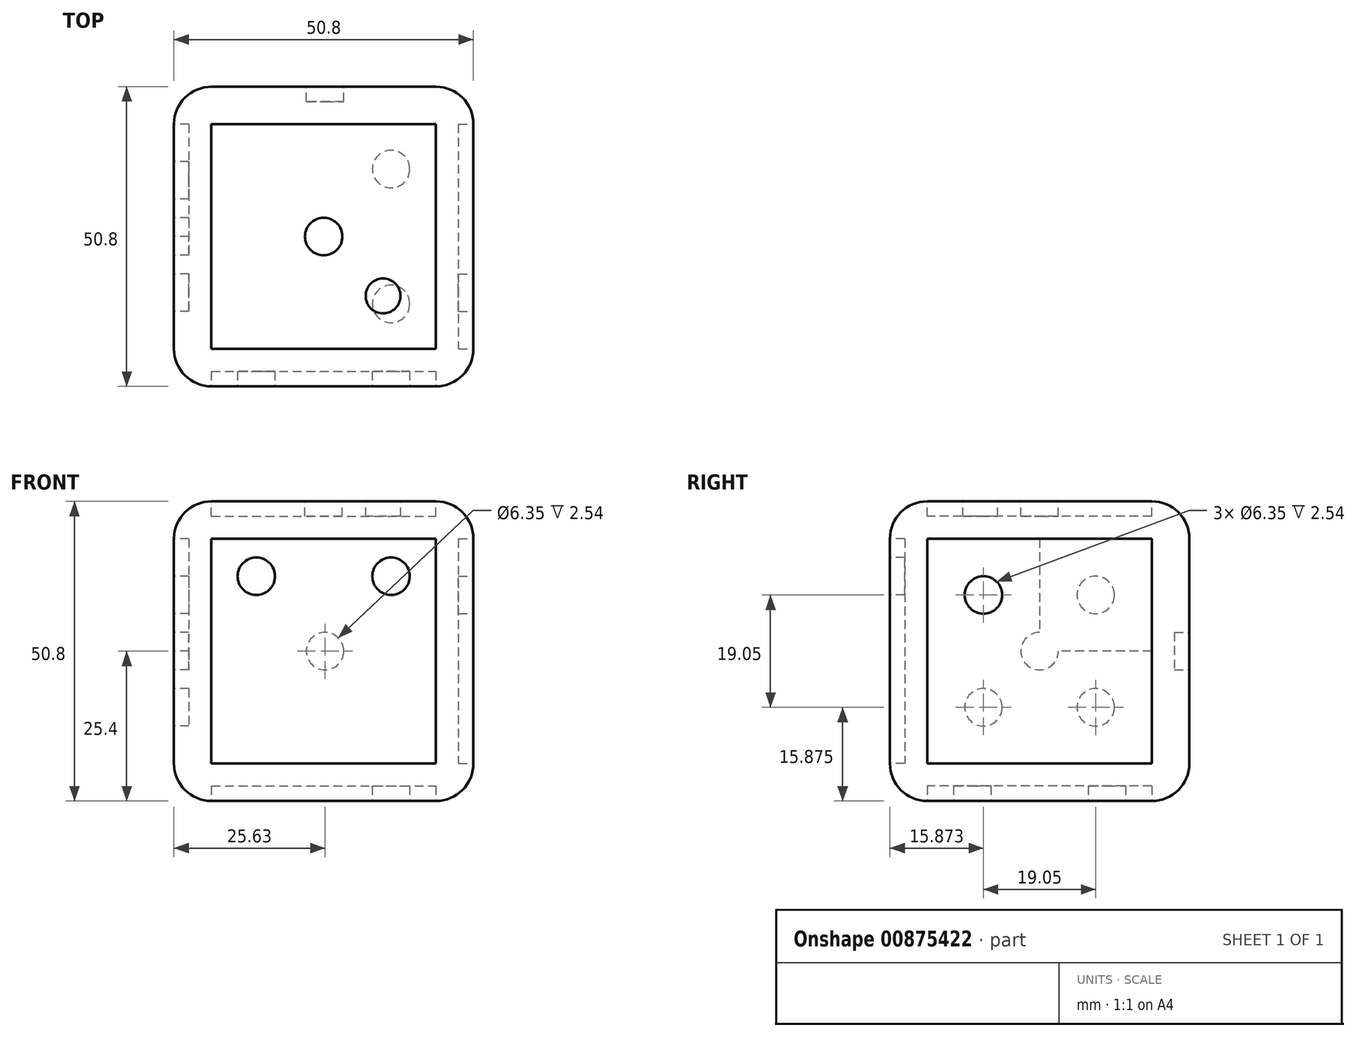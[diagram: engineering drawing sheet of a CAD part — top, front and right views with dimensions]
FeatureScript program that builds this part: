
annotation { "Feature Type Name" : "Feature", "Feature Type Description" : "" }
export const myFeature = defineFeature(function(context is Context, id is Id, definition is map)
    precondition{}
    {
        {
            var Q0;
            Q0=qCreatedBy(makeId("Top.planeOp"),FACE);
            var sketch = newSketch(context, id + "F0", { "sketchPlane" : qUnion([Q0])});
            skLineSegment(sketch, "E0.bottom", {"start": v(-25.63, 43.18) * mm, "end": v(25.17, 43.18) * mm});
            skLineSegment(sketch, "E0.top", {"start": v(-25.63, -7.62) * mm, "end": v(25.17, -7.62) * mm});
            skLineSegment(sketch, "E0.left", {"start": v(-25.63, 43.18) * mm, "end": v(-25.63, -7.62) * mm});
            skLineSegment(sketch, "E0.right", {"start": v(25.17, 43.18) * mm, "end": v(25.17, -7.62) * mm});
            skSolve(sketch);
        }
        {
            var Q0;
            Q0=makeQuery(id+"F0.imprint","IMPRINT",FACE,{"disambiguationData":[TD([[makeQuery(id+"F0.imprint","IMPRINT",EDGE,{"derivedFrom":sQuery(id+"F0.wireOp",EDGE,"E0.bottom")}),-1.0]])]});
            extrude(context, id + "F1", {"entities" : qUnion([Q0]), "depth" : 50.8 * mm, "offsetDistance" : 25.4 * mm});
        }
        {
            var Q0;
            Q0=makeQuery(id+"F1.opExtrude","SWEPT_EDGE",EDGE,{"disambiguationData":[OSD([sQuery(id+"F0.wireOp",EDGE,"E0.top"),sQuery(id+"F0.wireOp",EDGE,"E0.left")])]});
            var Q1;
            Q1=makeQuery(id+"F1.opExtrude","SWEPT_EDGE",EDGE,{"disambiguationData":[OSD([sQuery(id+"F0.wireOp",EDGE,"E0.top"),sQuery(id+"F0.wireOp",EDGE,"E0.right")])]});
            var Q2;
            Q2=makeQuery(id+"F1.opExtrude","CAP_EDGE",EDGE,{"disambiguationData":[OSD([sQuery(id+"F0.wireOp",EDGE,"E0.top")])],"isStart":true});
            var Q3;
            Q3=makeQuery(id+"F1.opExtrude","CAP_EDGE",EDGE,{"disambiguationData":[OSD([sQuery(id+"F0.wireOp",EDGE,"E0.top")])],"isStart":false});
            var Q4;
            Q4=makeQuery(id+"F1.opExtrude","SWEPT_EDGE",EDGE,{"disambiguationData":[OSD([sQuery(id+"F0.wireOp",EDGE,"E0.bottom"),sQuery(id+"F0.wireOp",EDGE,"E0.right")])]});
            var Q5;
            Q5=makeQuery(id+"F1.opExtrude","CAP_EDGE",EDGE,{"disambiguationData":[OSD([sQuery(id+"F0.wireOp",EDGE,"E0.right")])],"isStart":true});
            var Q6;
            Q6=makeQuery(id+"F1.opExtrude","SWEPT_EDGE",EDGE,{"disambiguationData":[OSD([sQuery(id+"F0.wireOp",EDGE,"E0.bottom"),sQuery(id+"F0.wireOp",EDGE,"E0.left")])]});
            var Q7;
            Q7=makeQuery(id+"F1.opExtrude","CAP_EDGE",EDGE,{"disambiguationData":[OSD([sQuery(id+"F0.wireOp",EDGE,"E0.right")])],"isStart":false});
            var Q8;
            Q8=makeQuery(id+"F1.opExtrude","CAP_EDGE",EDGE,{"disambiguationData":[OSD([sQuery(id+"F0.wireOp",EDGE,"E0.bottom")])],"isStart":true});
            var Q9;
            Q9=makeQuery(id+"F1.opExtrude","CAP_EDGE",EDGE,{"disambiguationData":[OSD([sQuery(id+"F0.wireOp",EDGE,"E0.left")])],"isStart":true});
            var Q10;
            Q10=makeQuery(id+"F1.opExtrude","CAP_EDGE",EDGE,{"disambiguationData":[OSD([sQuery(id+"F0.wireOp",EDGE,"E0.left")])],"isStart":false});
            var Q11;
            Q11=makeQuery(id+"F1.opExtrude","CAP_EDGE",EDGE,{"disambiguationData":[OSD([sQuery(id+"F0.wireOp",EDGE,"E0.bottom")])],"isStart":false});
            fillet(context, id + "F2", {"entities" : qUnion([Q0, Q1, Q2, Q3, Q4, Q5, Q6, Q7, Q8, Q9, Q10, Q11]), "radius" : 6.35 * mm, "tangentPropagation" : true, "allowEdgeOverflow" : false});
        }
        {
            var Q0;
            Q0=makeQuery(id+"F1.opExtrude","SWEPT_FACE",FACE,{"disambiguationData":[OSD([sQuery(id+"F0.wireOp",EDGE,"E0.bottom")])]});
            var sketch = newSketch(context, id + "F3", { "sketchPlane" : qUnion([Q0])});
            skLineSegment(sketch, "E1.0.0", {"start": v(-18.82, 44.45) * mm, "end": v(-18.82, 6.35) * mm});
            skLineSegment(sketch, "E1.0.1", {"start": v(-18.82, 6.35) * mm, "end": v(19.28, 6.35) * mm});
            skLineSegment(sketch, "E1.0.2", {"start": v(19.28, 6.35) * mm, "end": v(19.28, 44.45) * mm});
            skLineSegment(sketch, "E1.0.3", {"start": v(19.28, 44.45) * mm, "end": v(-18.82, 44.45) * mm});
            skLineSegment(sketch, "E2", {"start": v(19.28, 25.4) * mm, "end": v(-18.82, 25.4) * mm, "construction": true});
            skLineSegment(sketch, "E3", {"start": v(0, 44.45) * mm, "end": v(0, 6.35) * mm, "construction": true});
            skPoint(sketch, "E3.startSnap0", {"position": v(0.23, 44.45) * mm});
            skCircle(sketch, "E4", {"center": v(0, 25.4) * mm, "radius": 3.18 * mm});
            skSolve(sketch);
        }
        {
            var Q0;
            Q0=makeQuery(id+"F3.imprint","IMPRINT",FACE,{"disambiguationData":[TD([[makeQuery(id+"F3.imprint","IMPRINT",EDGE,{"derivedFrom":sQuery(id+"F3.wireOp",EDGE,"E4")}),1.0]])]});
            var Q1;
            Q1=sQuery(id+"F3.wireOp",EDGE,"E4");
            extrude(context, id + "F4", {"entities" : qUnion([Q0]), "operationType" : NewBodyOperationType.REMOVE, "surfaceEntities" : qUnion([Q1]), "oppositeDirection" : true, "depth" : 2.54 * mm, "offsetDistance" : 25.4 * mm});
        }
        {
            var Q0;
            Q0=makeQuery(id+"F1.opExtrude","SWEPT_FACE",FACE,{"disambiguationData":[OSD([sQuery(id+"F0.wireOp",EDGE,"E0.top")])]});
            var sketch = newSketch(context, id + "F5", { "sketchPlane" : qUnion([Q0])});
            skLineSegment(sketch, "E5.0.0", {"start": v(-19.28, 44.45) * mm, "end": v(-19.28, 6.35) * mm});
            skLineSegment(sketch, "E5.0.1", {"start": v(-19.28, 6.35) * mm, "end": v(18.82, 6.35) * mm});
            skLineSegment(sketch, "E5.0.2", {"start": v(18.82, 6.35) * mm, "end": v(18.82, 44.45) * mm});
            skLineSegment(sketch, "E5.0.3", {"start": v(18.82, 44.45) * mm, "end": v(-19.28, 44.45) * mm});
            skLineSegment(sketch, "E6", {"start": v(-11.66, 44.45) * mm, "end": v(-11.66, 6.35) * mm});
            skLineSegment(sketch, "E7", {"start": v(11.2, 44.45) * mm, "end": v(11.2, 6.35) * mm});
            skCircle(sketch, "E8", {"center": v(-11.66, 38.1) * mm, "radius": 3.18 * mm});
            skCircle(sketch, "E9", {"center": v(-11.66, 25.4) * mm, "radius": 3.18 * mm});
            skCircle(sketch, "E10", {"center": v(-11.66, 12.7) * mm, "radius": 3.18 * mm});
            skCircle(sketch, "E11", {"center": v(11.2, 25.4) * mm, "radius": 3.18 * mm});
            skCircle(sketch, "E12", {"center": v(11.2, 38.1) * mm, "radius": 3.18 * mm});
            skCircle(sketch, "E13", {"center": v(11.2, 12.7) * mm, "radius": 3.18 * mm});
            skSolve(sketch);
        }
        {
            var Q0;
            {var subQ0=sQuery(id+"F5.wireOp",EDGE,"E8");var subQ1=sQuery(id+"F5.wireOp",EDGE,"E6");var subQ2=makeQuery(id+"F5.imprint","INTERSECT",VERTEX,{"disambiguationData":[OD(0.0)],"derivedFrom":[subQ1,subQ0]});Q0=makeQuery(id+"F5.imprint","IMPRINT",FACE,{"disambiguationData":[TD([[makeQuery(id+"F5.imprint","IMPRINT",EDGE,{"disambiguationData":[TD([[subQ2,-1.0]])],"derivedFrom":subQ1}),-1.0]])]});}
            var Q1;
            {var subQ0=sQuery(id+"F5.wireOp",EDGE,"E8");var subQ1=sQuery(id+"F5.wireOp",EDGE,"E6");var subQ2=makeQuery(id+"F5.imprint","INTERSECT",VERTEX,{"disambiguationData":[OD(0.0)],"derivedFrom":[subQ1,subQ0]});Q1=makeQuery(id+"F5.imprint","IMPRINT",FACE,{"disambiguationData":[TD([[makeQuery(id+"F5.imprint","IMPRINT",EDGE,{"disambiguationData":[TD([[subQ2,-1.0]])],"derivedFrom":subQ1}),1.0]])]});}
            var Q2;
            {var subQ0=sQuery(id+"F5.wireOp",EDGE,"E9");var subQ1=sQuery(id+"F5.wireOp",EDGE,"E6");var subQ2=makeQuery(id+"F5.imprint","INTERSECT",VERTEX,{"disambiguationData":[OD(0.0)],"derivedFrom":[subQ1,subQ0]});Q2=makeQuery(id+"F5.imprint","IMPRINT",FACE,{"disambiguationData":[TD([[makeQuery(id+"F5.imprint","IMPRINT",EDGE,{"disambiguationData":[TD([[subQ2,-1.0]])],"derivedFrom":subQ1}),1.0]])]});}
            var Q3;
            {var subQ0=sQuery(id+"F5.wireOp",EDGE,"E9");var subQ1=sQuery(id+"F5.wireOp",EDGE,"E6");var subQ2=makeQuery(id+"F5.imprint","INTERSECT",VERTEX,{"disambiguationData":[OD(0.0)],"derivedFrom":[subQ1,subQ0]});Q3=makeQuery(id+"F5.imprint","IMPRINT",FACE,{"disambiguationData":[TD([[makeQuery(id+"F5.imprint","IMPRINT",EDGE,{"disambiguationData":[TD([[subQ2,-1.0]])],"derivedFrom":subQ1}),-1.0]])]});}
            var Q4;
            {var subQ0=sQuery(id+"F5.wireOp",EDGE,"E10");var subQ1=sQuery(id+"F5.wireOp",EDGE,"E6");var subQ2=makeQuery(id+"F5.imprint","INTERSECT",VERTEX,{"disambiguationData":[OD(0.0)],"derivedFrom":[subQ1,subQ0]});Q4=makeQuery(id+"F5.imprint","IMPRINT",FACE,{"disambiguationData":[TD([[makeQuery(id+"F5.imprint","IMPRINT",EDGE,{"disambiguationData":[TD([[subQ2,-1.0]])],"derivedFrom":subQ1}),1.0]])]});}
            var Q5;
            {var subQ0=sQuery(id+"F5.wireOp",EDGE,"E10");var subQ1=sQuery(id+"F5.wireOp",EDGE,"E6");var subQ2=makeQuery(id+"F5.imprint","INTERSECT",VERTEX,{"disambiguationData":[OD(0.0)],"derivedFrom":[subQ1,subQ0]});Q5=makeQuery(id+"F5.imprint","IMPRINT",FACE,{"disambiguationData":[TD([[makeQuery(id+"F5.imprint","IMPRINT",EDGE,{"disambiguationData":[TD([[subQ2,-1.0]])],"derivedFrom":subQ1}),-1.0]])]});}
            var Q6;
            {var subQ0=sQuery(id+"F5.wireOp",EDGE,"E13");var subQ1=sQuery(id+"F5.wireOp",EDGE,"E7");var subQ2=makeQuery(id+"F5.imprint","INTERSECT",VERTEX,{"disambiguationData":[OD(0.0)],"derivedFrom":[subQ1,subQ0]});Q6=makeQuery(id+"F5.imprint","IMPRINT",FACE,{"disambiguationData":[TD([[makeQuery(id+"F5.imprint","IMPRINT",EDGE,{"disambiguationData":[TD([[subQ2,-1.0]])],"derivedFrom":subQ1}),1.0]])]});}
            var Q7;
            {var subQ0=sQuery(id+"F5.wireOp",EDGE,"E13");var subQ1=sQuery(id+"F5.wireOp",EDGE,"E7");var subQ2=makeQuery(id+"F5.imprint","INTERSECT",VERTEX,{"disambiguationData":[OD(0.0)],"derivedFrom":[subQ1,subQ0]});Q7=makeQuery(id+"F5.imprint","IMPRINT",FACE,{"disambiguationData":[TD([[makeQuery(id+"F5.imprint","IMPRINT",EDGE,{"disambiguationData":[TD([[subQ2,-1.0]])],"derivedFrom":subQ1}),-1.0]])]});}
            var Q8;
            {var subQ0=sQuery(id+"F5.wireOp",EDGE,"E11");var subQ1=sQuery(id+"F5.wireOp",EDGE,"E7");var subQ2=makeQuery(id+"F5.imprint","INTERSECT",VERTEX,{"disambiguationData":[OD(0.0)],"derivedFrom":[subQ1,subQ0]});Q8=makeQuery(id+"F5.imprint","IMPRINT",FACE,{"disambiguationData":[TD([[makeQuery(id+"F5.imprint","IMPRINT",EDGE,{"disambiguationData":[TD([[subQ2,-1.0]])],"derivedFrom":subQ1}),1.0]])]});}
            var Q9;
            {var subQ0=sQuery(id+"F5.wireOp",EDGE,"E11");var subQ1=sQuery(id+"F5.wireOp",EDGE,"E7");var subQ2=makeQuery(id+"F5.imprint","INTERSECT",VERTEX,{"disambiguationData":[OD(0.0)],"derivedFrom":[subQ1,subQ0]});Q9=makeQuery(id+"F5.imprint","IMPRINT",FACE,{"disambiguationData":[TD([[makeQuery(id+"F5.imprint","IMPRINT",EDGE,{"disambiguationData":[TD([[subQ2,-1.0]])],"derivedFrom":subQ1}),-1.0]])]});}
            var Q10;
            {var subQ0=sQuery(id+"F5.wireOp",EDGE,"E12");var subQ1=sQuery(id+"F5.wireOp",EDGE,"E7");var subQ2=makeQuery(id+"F5.imprint","INTERSECT",VERTEX,{"disambiguationData":[OD(0.0)],"derivedFrom":[subQ1,subQ0]});Q10=makeQuery(id+"F5.imprint","IMPRINT",FACE,{"disambiguationData":[TD([[makeQuery(id+"F5.imprint","IMPRINT",EDGE,{"disambiguationData":[TD([[subQ2,-1.0]])],"derivedFrom":subQ1}),1.0]])]});}
            var Q11;
            {var subQ0=sQuery(id+"F5.wireOp",EDGE,"E12");var subQ1=sQuery(id+"F5.wireOp",EDGE,"E7");var subQ2=makeQuery(id+"F5.imprint","INTERSECT",VERTEX,{"disambiguationData":[OD(0.0)],"derivedFrom":[subQ1,subQ0]});Q11=makeQuery(id+"F5.imprint","IMPRINT",FACE,{"disambiguationData":[TD([[makeQuery(id+"F5.imprint","IMPRINT",EDGE,{"disambiguationData":[TD([[subQ2,-1.0]])],"derivedFrom":subQ1}),-1.0]])]});}
            extrude(context, id + "F6", {"entities" : qUnion([Q0, Q1, Q2, Q3, Q4, Q5, Q6, Q7, Q8, Q9, Q10, Q11]), "operationType" : NewBodyOperationType.REMOVE, "oppositeDirection" : true, "depth" : 2.54 * mm, "offsetDistance" : 25.4 * mm});
        }
        {
            var Q0;
            Q0=makeQuery(id+"F1.opExtrude","SWEPT_FACE",FACE,{"disambiguationData":[OSD([sQuery(id+"F0.wireOp",EDGE,"E0.left")])]});
            var sketch = newSketch(context, id + "F7", { "sketchPlane" : qUnion([Q0])});
            skLineSegment(sketch, "E14.0.0", {"start": v(-36.83, 44.45) * mm, "end": v(-36.83, 6.35) * mm});
            skLineSegment(sketch, "E14.0.1", {"start": v(-36.83, 6.35) * mm, "end": v(1.27, 6.35) * mm});
            skLineSegment(sketch, "E14.0.2", {"start": v(1.27, 6.35) * mm, "end": v(1.27, 44.45) * mm});
            skLineSegment(sketch, "E14.0.3", {"start": v(1.27, 44.45) * mm, "end": v(-36.83, 44.45) * mm});
            skLineSegment(sketch, "E15", {"start": v(-36.83, 25.4) * mm, "end": v(1.27, 25.4) * mm});
            skLineSegment(sketch, "E16", {"start": v(1.27, 25.4) * mm, "end": v(-17.78, 25.4) * mm});
            skLineSegment(sketch, "E17", {"start": v(-17.78, 44.45) * mm, "end": v(-17.78, 6.35) * mm});
            skCircle(sketch, "E18", {"center": v(-17.78, 25.4) * mm, "radius": 3.18 * mm});
            skLineSegment(sketch, "E19", {"start": v(-27.3, 44.45) * mm, "end": v(-27.3, 6.35) * mm});
            skLineSegment(sketch, "E20", {"start": v(-8.25, 44.45) * mm, "end": v(-8.25, 6.35) * mm});
            skCircle(sketch, "E21", {"center": v(-27.3, 34.93) * mm, "radius": 3.18 * mm});
            skCircle(sketch, "E22", {"center": v(-27.3, 15.88) * mm, "radius": 3.18 * mm});
            skCircle(sketch, "E23", {"center": v(-8.25, 34.93) * mm, "radius": 3.18 * mm});
            skCircle(sketch, "E24", {"center": v(-8.25, 15.88) * mm, "radius": 3.18 * mm});
            skSolve(sketch);
        }
        {
            var Q0;
            {var subQ0=sQuery(id+"F7.wireOp",EDGE,"E21");var subQ1=sQuery(id+"F7.wireOp",EDGE,"E19");var subQ2=makeQuery(id+"F7.imprint","INTERSECT",VERTEX,{"disambiguationData":[OD(0.0)],"derivedFrom":[subQ1,subQ0]});Q0=makeQuery(id+"F7.imprint","IMPRINT",FACE,{"disambiguationData":[TD([[makeQuery(id+"F7.imprint","IMPRINT",EDGE,{"disambiguationData":[TD([[subQ2,-1.0]])],"derivedFrom":subQ1}),1.0]])]});}
            var Q1;
            {var subQ0=sQuery(id+"F7.wireOp",EDGE,"E21");var subQ1=sQuery(id+"F7.wireOp",EDGE,"E19");var subQ2=makeQuery(id+"F7.imprint","INTERSECT",VERTEX,{"disambiguationData":[OD(0.0)],"derivedFrom":[subQ1,subQ0]});Q1=makeQuery(id+"F7.imprint","IMPRINT",FACE,{"disambiguationData":[TD([[makeQuery(id+"F7.imprint","IMPRINT",EDGE,{"disambiguationData":[TD([[subQ2,-1.0]])],"derivedFrom":subQ1}),-1.0]])]});}
            var Q2;
            {var subQ0=sQuery(id+"F7.wireOp",EDGE,"E23");var subQ1=sQuery(id+"F7.wireOp",EDGE,"E20");var subQ2=makeQuery(id+"F7.imprint","INTERSECT",VERTEX,{"disambiguationData":[OD(0.0)],"derivedFrom":[subQ1,subQ0]});Q2=makeQuery(id+"F7.imprint","IMPRINT",FACE,{"disambiguationData":[TD([[makeQuery(id+"F7.imprint","IMPRINT",EDGE,{"disambiguationData":[TD([[subQ2,-1.0]])],"derivedFrom":subQ1}),-1.0]])]});}
            var Q3;
            {var subQ0=sQuery(id+"F7.wireOp",EDGE,"E23");var subQ1=sQuery(id+"F7.wireOp",EDGE,"E20");var subQ2=makeQuery(id+"F7.imprint","INTERSECT",VERTEX,{"disambiguationData":[OD(0.0)],"derivedFrom":[subQ1,subQ0]});Q3=makeQuery(id+"F7.imprint","IMPRINT",FACE,{"disambiguationData":[TD([[makeQuery(id+"F7.imprint","IMPRINT",EDGE,{"disambiguationData":[TD([[subQ2,-1.0]])],"derivedFrom":subQ1}),1.0]])]});}
            var Q4;
            {var subQ1=sQuery(id+"F7.wireOp",EDGE,"E16");var subQ3=sQuery(id+"F7.wireOp",EDGE,"E18");var subQ4=makeQuery(id+"F7.imprint","INTERSECT",VERTEX,{"derivedFrom":[subQ1,subQ3]});Q4=makeQuery(id+"F7.imprint","IMPRINT",FACE,{"disambiguationData":[TD([[makeQuery(id+"F7.imprint","IMPRINT",EDGE,{"disambiguationData":[TD([[subQ4,-1.0]])],"derivedFrom":subQ3}),1.0]])]});}
            var Q5;
            {var subQ1=sQuery(id+"F7.wireOp",EDGE,"E16");var subQ3=sQuery(id+"F7.wireOp",EDGE,"E18");var subQ4=makeQuery(id+"F7.imprint","INTERSECT",VERTEX,{"derivedFrom":[subQ1,subQ3]});Q5=makeQuery(id+"F7.imprint","IMPRINT",FACE,{"disambiguationData":[TD([[makeQuery(id+"F7.imprint","IMPRINT",EDGE,{"disambiguationData":[TD([[subQ4,1.0]])],"derivedFrom":subQ3}),1.0]])]});}
            var Q6;
            {var subQ1=sQuery(id+"F7.wireOp",EDGE,"E15");var subQ3=sQuery(id+"F7.wireOp",EDGE,"E18");var subQ4=makeQuery(id+"F7.imprint","INTERSECT",VERTEX,{"derivedFrom":[subQ1,subQ3]});Q6=makeQuery(id+"F7.imprint","IMPRINT",FACE,{"disambiguationData":[TD([[makeQuery(id+"F7.imprint","IMPRINT",EDGE,{"disambiguationData":[TD([[subQ4,-1.0]])],"derivedFrom":subQ3}),1.0]])]});}
            var Q7;
            {var subQ1=sQuery(id+"F7.wireOp",EDGE,"E15");var subQ3=sQuery(id+"F7.wireOp",EDGE,"E18");var subQ4=makeQuery(id+"F7.imprint","INTERSECT",VERTEX,{"derivedFrom":[subQ1,subQ3]});Q7=makeQuery(id+"F7.imprint","IMPRINT",FACE,{"disambiguationData":[TD([[makeQuery(id+"F7.imprint","IMPRINT",EDGE,{"disambiguationData":[TD([[subQ4,1.0]])],"derivedFrom":subQ3}),1.0]])]});}
            var Q8;
            {var subQ0=sQuery(id+"F7.wireOp",EDGE,"E24");var subQ1=sQuery(id+"F7.wireOp",EDGE,"E20");var subQ2=makeQuery(id+"F7.imprint","INTERSECT",VERTEX,{"disambiguationData":[OD(0.0)],"derivedFrom":[subQ1,subQ0]});Q8=makeQuery(id+"F7.imprint","IMPRINT",FACE,{"disambiguationData":[TD([[makeQuery(id+"F7.imprint","IMPRINT",EDGE,{"disambiguationData":[TD([[subQ2,-1.0]])],"derivedFrom":subQ1}),1.0]])]});}
            var Q9;
            {var subQ0=sQuery(id+"F7.wireOp",EDGE,"E24");var subQ1=sQuery(id+"F7.wireOp",EDGE,"E20");var subQ2=makeQuery(id+"F7.imprint","INTERSECT",VERTEX,{"disambiguationData":[OD(0.0)],"derivedFrom":[subQ1,subQ0]});Q9=makeQuery(id+"F7.imprint","IMPRINT",FACE,{"disambiguationData":[TD([[makeQuery(id+"F7.imprint","IMPRINT",EDGE,{"disambiguationData":[TD([[subQ2,-1.0]])],"derivedFrom":subQ1}),-1.0]])]});}
            var Q10;
            {var subQ0=sQuery(id+"F7.wireOp",EDGE,"E22");var subQ1=sQuery(id+"F7.wireOp",EDGE,"E19");var subQ2=makeQuery(id+"F7.imprint","INTERSECT",VERTEX,{"disambiguationData":[OD(0.0)],"derivedFrom":[subQ1,subQ0]});Q10=makeQuery(id+"F7.imprint","IMPRINT",FACE,{"disambiguationData":[TD([[makeQuery(id+"F7.imprint","IMPRINT",EDGE,{"disambiguationData":[TD([[subQ2,-1.0]])],"derivedFrom":subQ1}),1.0]])]});}
            var Q11;
            {var subQ0=sQuery(id+"F7.wireOp",EDGE,"E22");var subQ1=sQuery(id+"F7.wireOp",EDGE,"E19");var subQ2=makeQuery(id+"F7.imprint","INTERSECT",VERTEX,{"disambiguationData":[OD(0.0)],"derivedFrom":[subQ1,subQ0]});Q11=makeQuery(id+"F7.imprint","IMPRINT",FACE,{"disambiguationData":[TD([[makeQuery(id+"F7.imprint","IMPRINT",EDGE,{"disambiguationData":[TD([[subQ2,-1.0]])],"derivedFrom":subQ1}),-1.0]])]});}
            extrude(context, id + "F8", {"entities" : qUnion([Q0, Q1, Q2, Q3, Q4, Q5, Q6, Q7, Q8, Q9, Q10, Q11]), "operationType" : NewBodyOperationType.REMOVE, "oppositeDirection" : true, "depth" : 2.54 * mm, "offsetDistance" : 25.4 * mm});
        }
        {
            var Q0;
            Q0=makeQuery(id+"F1.opExtrude","SWEPT_FACE",FACE,{"disambiguationData":[OSD([sQuery(id+"F0.wireOp",EDGE,"E0.right")])]});
            var sketch = newSketch(context, id + "F9", { "sketchPlane" : qUnion([Q0])});
            skLineSegment(sketch, "E25", {"start": v(-1.27, 44.45) * mm, "end": v(36.83, 6.35) * mm});
            skCircle(sketch, "E26", {"center": v(27.3, 15.87) * mm, "radius": 3.18 * mm});
            skCircle(sketch, "E27", {"center": v(8.25, 34.93) * mm, "radius": 3.18 * mm});
            skSolve(sketch);
        }
        {
            var Q0;
            {var subQ0=sQuery(id+"F9.wireOp",EDGE,"E26");var subQ1=sQuery(id+"F9.wireOp",EDGE,"E25");var subQ2=makeQuery(id+"F9.imprint","INTERSECT",VERTEX,{"disambiguationData":[OD(0.0)],"derivedFrom":[subQ1,subQ0]});Q0=makeQuery(id+"F9.imprint","IMPRINT",FACE,{"disambiguationData":[TD([[makeQuery(id+"F9.imprint","IMPRINT",EDGE,{"disambiguationData":[TD([[subQ2,-1.0]])],"derivedFrom":subQ1}),1.0]])]});}
            var Q1;
            {var subQ0=sQuery(id+"F9.wireOp",EDGE,"E26");var subQ1=sQuery(id+"F9.wireOp",EDGE,"E25");var subQ2=makeQuery(id+"F9.imprint","INTERSECT",VERTEX,{"disambiguationData":[OD(0.0)],"derivedFrom":[subQ1,subQ0]});Q1=makeQuery(id+"F9.imprint","IMPRINT",FACE,{"disambiguationData":[TD([[makeQuery(id+"F9.imprint","IMPRINT",EDGE,{"disambiguationData":[TD([[subQ2,-1.0]])],"derivedFrom":subQ1}),-1.0]])]});}
            var Q2;
            {var subQ0=sQuery(id+"F9.wireOp",EDGE,"E27");var subQ1=sQuery(id+"F9.wireOp",EDGE,"E25");var subQ2=makeQuery(id+"F9.imprint","INTERSECT",VERTEX,{"disambiguationData":[OD(0.0)],"derivedFrom":[subQ1,subQ0]});Q2=makeQuery(id+"F9.imprint","IMPRINT",FACE,{"disambiguationData":[TD([[makeQuery(id+"F9.imprint","IMPRINT",EDGE,{"disambiguationData":[TD([[subQ2,-1.0]])],"derivedFrom":subQ1}),-1.0]])]});}
            var Q3;
            {var subQ0=sQuery(id+"F9.wireOp",EDGE,"E27");var subQ1=sQuery(id+"F9.wireOp",EDGE,"E25");var subQ2=makeQuery(id+"F9.imprint","INTERSECT",VERTEX,{"disambiguationData":[OD(0.0)],"derivedFrom":[subQ1,subQ0]});Q3=makeQuery(id+"F9.imprint","IMPRINT",FACE,{"disambiguationData":[TD([[makeQuery(id+"F9.imprint","IMPRINT",EDGE,{"disambiguationData":[TD([[subQ2,-1.0]])],"derivedFrom":subQ1}),1.0]])]});}
            extrude(context, id + "F10", {"entities" : qUnion([Q0, Q1, Q2, Q3]), "operationType" : NewBodyOperationType.REMOVE, "oppositeDirection" : true, "depth" : 2.54 * mm, "offsetDistance" : 25.4 * mm});
        }
        {
            var Q0;
            Q0=makeQuery(id+"F1.opExtrude","CAP_FACE",FACE,{"disambiguationData":[OSD([sQuery(id+"F0.wireOp",EDGE,"E0.bottom"),sQuery(id+"F0.wireOp",EDGE,"E0.top"),sQuery(id+"F0.wireOp",EDGE,"E0.left"),sQuery(id+"F0.wireOp",EDGE,"E0.right")])],"isStart":true});
            var sketch = newSketch(context, id + "F11", { "sketchPlane" : qUnion([Q0])});
            skLineSegment(sketch, "E28.0.0", {"start": v(-19.28, -36.83) * mm, "end": v(18.82, -36.83) * mm});
            skLineSegment(sketch, "E28.0.1", {"start": v(18.82, -36.83) * mm, "end": v(18.82, 1.27) * mm});
            skLineSegment(sketch, "E28.0.2", {"start": v(18.82, 1.27) * mm, "end": v(-19.28, 1.27) * mm});
            skLineSegment(sketch, "E28.0.3", {"start": v(-19.28, 1.27) * mm, "end": v(-19.28, -36.83) * mm});
            skLineSegment(sketch, "E29", {"start": v(18.82, -6.35) * mm, "end": v(-19.28, -6.35) * mm});
            skLineSegment(sketch, "E30", {"start": v(18.82, -29.2) * mm, "end": v(-19.28, -29.2) * mm});
            skCircle(sketch, "E31", {"center": v(11.2, -6.35) * mm, "radius": 3.18 * mm});
            skCircle(sketch, "E32", {"center": v(-11.66, -6.35) * mm, "radius": 3.18 * mm});
            skCircle(sketch, "E33", {"center": v(-11.66, -29.2) * mm, "radius": 3.18 * mm});
            skCircle(sketch, "E34", {"center": v(11.2, -29.2) * mm, "radius": 3.18 * mm});
            skSolve(sketch);
        }
        {
            var Q0;
            {var subQ0=sQuery(id+"F11.wireOp",EDGE,"E31");var subQ1=sQuery(id+"F11.wireOp",EDGE,"E29");var subQ2=makeQuery(id+"F11.imprint","INTERSECT",VERTEX,{"disambiguationData":[OD(0.0)],"derivedFrom":[subQ1,subQ0]});Q0=makeQuery(id+"F11.imprint","IMPRINT",FACE,{"disambiguationData":[TD([[makeQuery(id+"F11.imprint","IMPRINT",EDGE,{"disambiguationData":[TD([[subQ2,-1.0]])],"derivedFrom":subQ1}),-1.0]])]});}
            var Q1;
            {var subQ0=sQuery(id+"F11.wireOp",EDGE,"E31");var subQ1=sQuery(id+"F11.wireOp",EDGE,"E29");var subQ2=makeQuery(id+"F11.imprint","INTERSECT",VERTEX,{"disambiguationData":[OD(0.0)],"derivedFrom":[subQ1,subQ0]});Q1=makeQuery(id+"F11.imprint","IMPRINT",FACE,{"disambiguationData":[TD([[makeQuery(id+"F11.imprint","IMPRINT",EDGE,{"disambiguationData":[TD([[subQ2,-1.0]])],"derivedFrom":subQ1}),1.0]])]});}
            var Q2;
            {var subQ0=sQuery(id+"F11.wireOp",EDGE,"E34");var subQ1=sQuery(id+"F11.wireOp",EDGE,"E30");var subQ2=makeQuery(id+"F11.imprint","INTERSECT",VERTEX,{"disambiguationData":[OD(0.0)],"derivedFrom":[subQ1,subQ0]});Q2=makeQuery(id+"F11.imprint","IMPRINT",FACE,{"disambiguationData":[TD([[makeQuery(id+"F11.imprint","IMPRINT",EDGE,{"disambiguationData":[TD([[subQ2,-1.0]])],"derivedFrom":subQ1}),-1.0]])]});}
            var Q3;
            {var subQ0=sQuery(id+"F11.wireOp",EDGE,"E34");var subQ1=sQuery(id+"F11.wireOp",EDGE,"E30");var subQ2=makeQuery(id+"F11.imprint","INTERSECT",VERTEX,{"disambiguationData":[OD(0.0)],"derivedFrom":[subQ1,subQ0]});Q3=makeQuery(id+"F11.imprint","IMPRINT",FACE,{"disambiguationData":[TD([[makeQuery(id+"F11.imprint","IMPRINT",EDGE,{"disambiguationData":[TD([[subQ2,-1.0]])],"derivedFrom":subQ1}),1.0]])]});}
            var Q4;
            {var subQ0=sQuery(id+"F11.wireOp",EDGE,"E33");var subQ1=sQuery(id+"F11.wireOp",EDGE,"E30");var subQ2=makeQuery(id+"F11.imprint","INTERSECT",VERTEX,{"disambiguationData":[OD(0.0)],"derivedFrom":[subQ1,subQ0]});Q4=makeQuery(id+"F11.imprint","IMPRINT",FACE,{"disambiguationData":[TD([[makeQuery(id+"F11.imprint","IMPRINT",EDGE,{"disambiguationData":[TD([[subQ2,-1.0]])],"derivedFrom":subQ1}),1.0]])]});}
            var Q5;
            {var subQ0=sQuery(id+"F11.wireOp",EDGE,"E33");var subQ1=sQuery(id+"F11.wireOp",EDGE,"E30");var subQ2=makeQuery(id+"F11.imprint","INTERSECT",VERTEX,{"disambiguationData":[OD(0.0)],"derivedFrom":[subQ1,subQ0]});Q5=makeQuery(id+"F11.imprint","IMPRINT",FACE,{"disambiguationData":[TD([[makeQuery(id+"F11.imprint","IMPRINT",EDGE,{"disambiguationData":[TD([[subQ2,-1.0]])],"derivedFrom":subQ1}),-1.0]])]});}
            var Q6;
            {var subQ0=sQuery(id+"F11.wireOp",EDGE,"E32");var subQ1=sQuery(id+"F11.wireOp",EDGE,"E29");var subQ2=makeQuery(id+"F11.imprint","INTERSECT",VERTEX,{"disambiguationData":[OD(0.0)],"derivedFrom":[subQ1,subQ0]});Q6=makeQuery(id+"F11.imprint","IMPRINT",FACE,{"disambiguationData":[TD([[makeQuery(id+"F11.imprint","IMPRINT",EDGE,{"disambiguationData":[TD([[subQ2,-1.0]])],"derivedFrom":subQ1}),1.0]])]});}
            var Q7;
            {var subQ0=sQuery(id+"F11.wireOp",EDGE,"E32");var subQ1=sQuery(id+"F11.wireOp",EDGE,"E29");var subQ2=makeQuery(id+"F11.imprint","INTERSECT",VERTEX,{"disambiguationData":[OD(0.0)],"derivedFrom":[subQ1,subQ0]});Q7=makeQuery(id+"F11.imprint","IMPRINT",FACE,{"disambiguationData":[TD([[makeQuery(id+"F11.imprint","IMPRINT",EDGE,{"disambiguationData":[TD([[subQ2,-1.0]])],"derivedFrom":subQ1}),-1.0]])]});}
            extrude(context, id + "F12", {"entities" : qUnion([Q0, Q1, Q2, Q3, Q4, Q5, Q6, Q7]), "operationType" : NewBodyOperationType.REMOVE, "oppositeDirection" : true, "depth" : 2.54 * mm, "offsetDistance" : 25.4 * mm});
        }
        {
            var Q0;
            Q0=makeQuery(id+"F1.opExtrude","CAP_FACE",FACE,{"disambiguationData":[OSD([sQuery(id+"F0.wireOp",EDGE,"E0.bottom"),sQuery(id+"F0.wireOp",EDGE,"E0.top"),sQuery(id+"F0.wireOp",EDGE,"E0.left"),sQuery(id+"F0.wireOp",EDGE,"E0.right")])],"isStart":false});
            var sketch = newSketch(context, id + "F13", { "sketchPlane" : qUnion([Q0])});
            skLineSegment(sketch, "E35", {"start": v(-19.28, 36.83) * mm, "end": v(18.82, -1.27) * mm});
            skCircle(sketch, "E36", {"center": v(-10.3, 27.85) * mm, "radius": 3.18 * mm});
            skCircle(sketch, "E37", {"center": v(-0.23, 17.78) * mm, "radius": 3.18 * mm});
            skCircle(sketch, "E38", {"center": v(9.85, 7.7) * mm, "radius": 2.95 * mm});
            skSolve(sketch);
        }
        {
            var Q0;
            {var subQ0=sQuery(id+"F13.wireOp",EDGE,"E37");var subQ1=sQuery(id+"F13.wireOp",EDGE,"E35");var subQ2=makeQuery(id+"F13.imprint","INTERSECT",VERTEX,{"disambiguationData":[OD(0.0)],"derivedFrom":[subQ1,subQ0]});Q0=makeQuery(id+"F13.imprint","IMPRINT",FACE,{"disambiguationData":[TD([[makeQuery(id+"F13.imprint","IMPRINT",EDGE,{"disambiguationData":[TD([[subQ2,-1.0]])],"derivedFrom":subQ1}),-1.0]])]});}
            var Q1;
            {var subQ0=sQuery(id+"F13.wireOp",EDGE,"E37");var subQ1=sQuery(id+"F13.wireOp",EDGE,"E35");var subQ2=makeQuery(id+"F13.imprint","INTERSECT",VERTEX,{"disambiguationData":[OD(0.0)],"derivedFrom":[subQ1,subQ0]});Q1=makeQuery(id+"F13.imprint","IMPRINT",FACE,{"disambiguationData":[TD([[makeQuery(id+"F13.imprint","IMPRINT",EDGE,{"disambiguationData":[TD([[subQ2,-1.0]])],"derivedFrom":subQ1}),1.0]])]});}
            var Q2;
            {var subQ0=sQuery(id+"F13.wireOp",EDGE,"E36");var subQ1=sQuery(id+"F13.wireOp",EDGE,"E35");var subQ2=makeQuery(id+"F13.imprint","INTERSECT",VERTEX,{"disambiguationData":[OD(0.0)],"derivedFrom":[subQ1,subQ0]});Q2=makeQuery(id+"F13.imprint","IMPRINT",FACE,{"disambiguationData":[TD([[makeQuery(id+"F13.imprint","IMPRINT",EDGE,{"disambiguationData":[TD([[subQ2,-1.0]])],"derivedFrom":subQ1}),1.0]])]});}
            var Q3;
            {var subQ0=sQuery(id+"F13.wireOp",EDGE,"E36");var subQ1=sQuery(id+"F13.wireOp",EDGE,"E35");var subQ2=makeQuery(id+"F13.imprint","INTERSECT",VERTEX,{"disambiguationData":[OD(0.0)],"derivedFrom":[subQ1,subQ0]});Q3=makeQuery(id+"F13.imprint","IMPRINT",FACE,{"disambiguationData":[TD([[makeQuery(id+"F13.imprint","IMPRINT",EDGE,{"disambiguationData":[TD([[subQ2,-1.0]])],"derivedFrom":subQ1}),-1.0]])]});}
            var Q4;
            {var subQ0=sQuery(id+"F13.wireOp",EDGE,"E38");var subQ1=sQuery(id+"F13.wireOp",EDGE,"E35");var subQ2=makeQuery(id+"F13.imprint","INTERSECT",VERTEX,{"disambiguationData":[OD(0.0)],"derivedFrom":[subQ1,subQ0]});Q4=makeQuery(id+"F13.imprint","IMPRINT",FACE,{"disambiguationData":[TD([[makeQuery(id+"F13.imprint","IMPRINT",EDGE,{"disambiguationData":[TD([[subQ2,-1.0]])],"derivedFrom":subQ1}),1.0]])]});}
            var Q5;
            {var subQ0=sQuery(id+"F13.wireOp",EDGE,"E38");var subQ1=sQuery(id+"F13.wireOp",EDGE,"E35");var subQ2=makeQuery(id+"F13.imprint","INTERSECT",VERTEX,{"disambiguationData":[OD(0.0)],"derivedFrom":[subQ1,subQ0]});Q5=makeQuery(id+"F13.imprint","IMPRINT",FACE,{"disambiguationData":[TD([[makeQuery(id+"F13.imprint","IMPRINT",EDGE,{"disambiguationData":[TD([[subQ2,-1.0]])],"derivedFrom":subQ1}),-1.0]])]});}
            extrude(context, id + "F14", {"entities" : qUnion([Q0, Q1, Q2, Q3, Q4, Q5]), "operationType" : NewBodyOperationType.REMOVE, "oppositeDirection" : true, "depth" : 2.54 * mm, "offsetDistance" : 25.4 * mm});
        }
    });
